# Revit family: Screen_Schiavello_Toku
name_source: partatom
category: Furniture
units: mm (PartAtom-declared; Revit-internal decimal feet)

## family parameters
Always vertical = Yes
Cut with Voids When Loaded = No
OmniClass Number = 23.40.70.14.64.11
Room Calculation Point = No
Shared = No
Work Plane-Based = No

## types (2) — shared parameters
Description = Named after the Japanese word for ‘talk’, Toku inspires people to connect, converse and collaborate, while also createing spaces for privacy and focus, communication and collaboration.
Manufacturer = Schiavello
ManufacturerOverallDepth = 220 mm  [stored 0.721785 ft]
ManufacturerOverallHeight = 1200 mm
ManufacturerOverallWidth = 1200 mm
ManufacturerURLProductSpecific = https://www.schiavello.com
ModifiedIssue = 20200129 $
URL = https://www.schiavello.com

## per-type parameters (varying)
| type | Mesh | Model | Type Comments | Upholstery | UpholsteryTopMaterial |
| Upholstered | No | Toku - Screen - Upholstered | Toku - Screen - Upholstered | Yes | Fabric_Schiavello_Revive1_0154 |
| Mesh | Yes | Toku - Screen - Mesh | Toku - Screen - Mesh | No | Fabric_Schiavello_Revive1_0944 |

note: [stored X ft] marks values corroborated as IEEE doubles in the binary element streams (Revit-internal decimal feet)

## geometry (parser evidence)
native form markers: Sweep x2
no freeform markers — native parametric forms only
